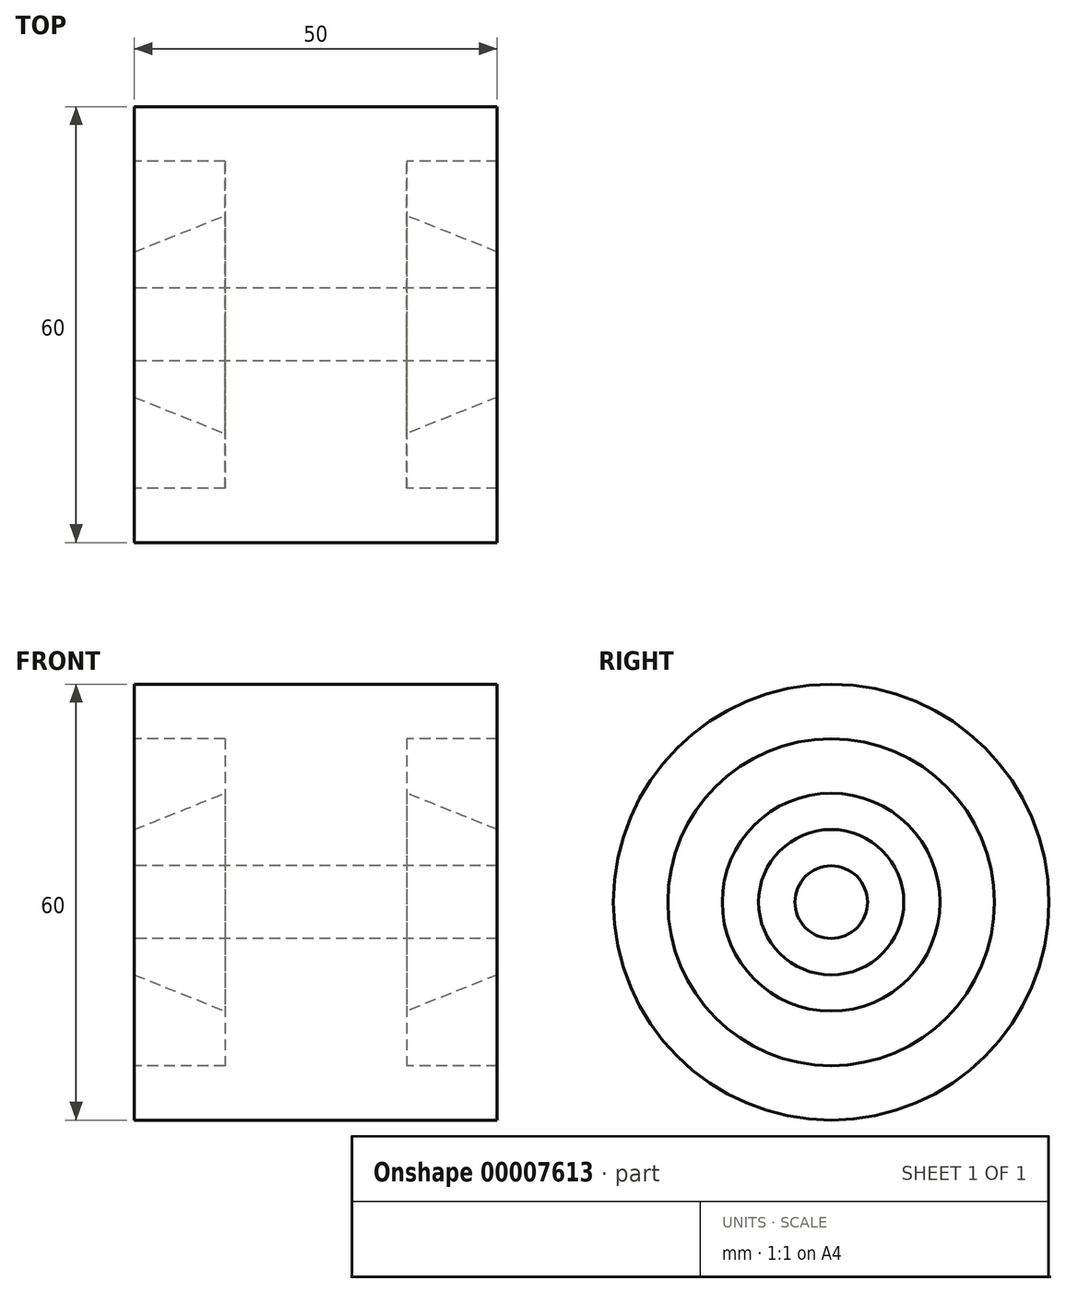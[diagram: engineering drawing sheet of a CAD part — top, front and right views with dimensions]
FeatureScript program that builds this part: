
annotation { "Feature Type Name" : "Feature", "Feature Type Description" : "" }
export const myFeature = defineFeature(function(context is Context, id is Id, definition is map)
    precondition{}
    {
        {
            var Q0;
            Q0=qCreatedBy(makeId("Front.planeOp"),FACE);
            var sketch = newSketch(context, id + "F0", { "sketchPlane" : qUnion([Q0])});
            skLineSegment(sketch, "E0", {"start": v(-25, 0) * mm, "end": v(25, 0) * mm, "construction": true});
            skLineSegment(sketch, "E1", {"start": v(-25, -5) * mm, "end": v(25, -5) * mm});
            skLineSegment(sketch, "E2", {"start": v(25, -5) * mm, "end": v(25, -10) * mm});
            skLineSegment(sketch, "E3", {"start": v(25, -10) * mm, "end": v(12.5, -15) * mm});
            skLineSegment(sketch, "E4", {"start": v(12.5, -15) * mm, "end": v(12.5, -22.5) * mm});
            skLineSegment(sketch, "E5", {"start": v(12.5, -22.5) * mm, "end": v(25, -22.5) * mm});
            skLineSegment(sketch, "E6", {"start": v(25, -22.5) * mm, "end": v(25, -30) * mm});
            skLineSegment(sketch, "E7", {"start": v(25, -30) * mm, "end": v(-25, -30) * mm});
            skLineSegment(sketch, "E8", {"start": v(-25, -30) * mm, "end": v(-25, -22.5) * mm});
            skLineSegment(sketch, "E9", {"start": v(-25, -22.5) * mm, "end": v(-12.5, -22.5) * mm});
            skLineSegment(sketch, "E10", {"start": v(-12.5, -22.5) * mm, "end": v(-12.5, -15) * mm});
            skLineSegment(sketch, "E11", {"start": v(-12.5, -15) * mm, "end": v(-25, -10) * mm});
            skLineSegment(sketch, "E12", {"start": v(-25, -10) * mm, "end": v(-25, -5) * mm});
            skSolve(sketch);
        }
        {
            var Q0;
            Q0 = qSketchRegion(id + "F0", true);
            var Q1;
            Q1=sQuery(id+"F0.wireOp",EDGE,"E0");
            revolve(context, id + "F1", {"entities" : qUnion([Q0]), "axis" : qUnion([Q1]), "revolveType" : RevolveType.FULL});
        }
    });
